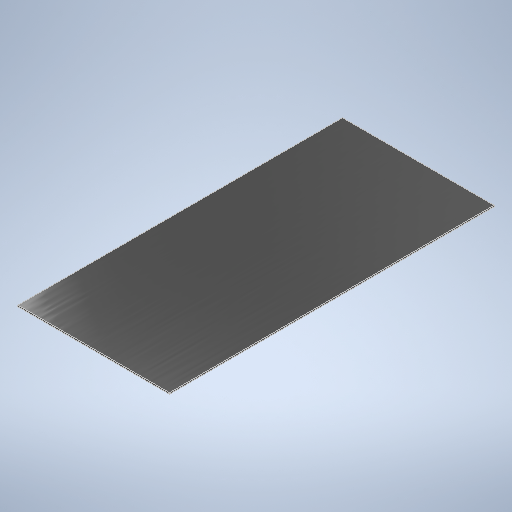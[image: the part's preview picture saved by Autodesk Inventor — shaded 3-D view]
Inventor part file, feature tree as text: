
AUTODESK INVENTOR PART (.ipt)
format: ipt  version: 2025.1 (Build 291241020, 241B)  size: 237,056 bytes
history: native  units: in
note: dims shown in document units (in); Inventor stores cm internally (conversion verified against a paired STEP export)
features: extrude x1, sketch x1
ambient origin geometry x8: Origin, YZ Plane, XZ Plane, XY Plane, X Axis, Y Axis, Z Axis, Center Point
bodies: Solid1 (feature_tree)
feature tree (2):
  extrude  "Extrusion1"  Depth=28.375in
  sketch  "Sketch1"  dims[d0=13.25in d1=28.375in d2=0.125in d3=0.0in]
